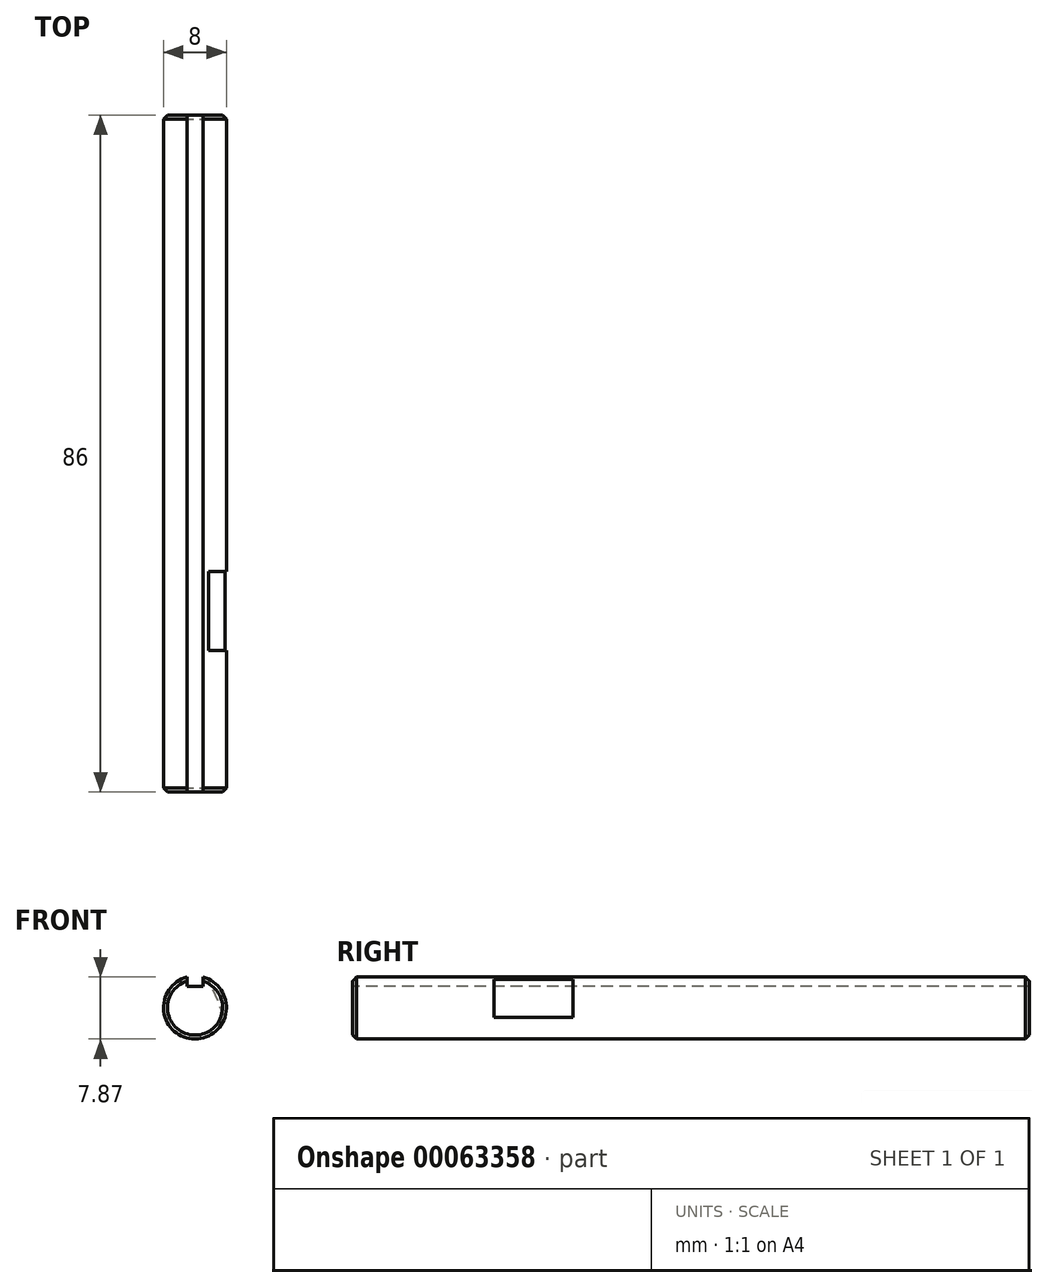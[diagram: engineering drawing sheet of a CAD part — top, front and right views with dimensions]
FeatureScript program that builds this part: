
annotation { "Feature Type Name" : "Feature", "Feature Type Description" : "" }
export const myFeature = defineFeature(function(context is Context, id is Id, definition is map)
    precondition{}
    {
        {
            var Q0;
            Q0=qCreatedBy(makeId("Front.planeOp"),FACE);
            var sketch = newSketch(context, id + "F0", { "sketchPlane" : qUnion([Q0])});
            skCircle(sketch, "E0", {"center": v(0, 0) * mm, "radius": 4 * mm});
            skSolve(sketch);
        }
        {
            var Q0;
            Q0=qSketchRegion(id+"F0",true);
            extrude(context, id + "F1", {"entities" : qUnion([Q0]), "depth" : 86 * mm});
        }
        {
            var Q0;
            Q0=makeQuery(id+"F1.opExtrude","CAP_FACE",FACE,{"disambiguationData":[OSD([sQuery(id+"F0.wireOp",EDGE,"E0")])],"isStart":false});
            var sketch = newSketch(context, id + "F2", { "sketchPlane" : qUnion([Q0])});
            skLineSegment(sketch, "E1", {"start": v(-1, 5.35) * mm, "end": v(1, 5.35) * mm});
            skLineSegment(sketch, "E2", {"start": v(0, 0) * mm, "end": v(0, 5.35) * mm, "construction": true});
            skLineSegment(sketch, "E3", {"start": v(-1, 2.67) * mm, "end": v(1, 2.67) * mm});
            skPoint(sketch, "E3.startSnap0", {"position": v(0, 2.67) * mm});
            skLineSegment(sketch, "E4", {"start": v(1, 2.67) * mm, "end": v(1, 5.35) * mm});
            skLineSegment(sketch, "E5", {"start": v(-1, 2.67) * mm, "end": v(-1, 5.35) * mm});
            skLineSegment(sketch, "E6", {"start": v(1, 3.87) * mm, "end": v(-1, 3.87) * mm, "construction": true});
            skSolve(sketch);
        }
        {
            var Q0;
            Q0=qSketchRegion(id+"F2",true);
            extrude(context, id + "F3", {"entities" : qUnion([Q0]), "operationType" : NewBodyOperationType.REMOVE, "endBound" : BoundingType.THROUGH_ALL, "oppositeDirection" : true, "depth" : 25 * mm});
        }
        {
            var Q0;
            Q0=makeQuery(id+"F1.opExtrude","CAP_EDGE",EDGE,{"disambiguationData":[OSD([sQuery(id+"F0.wireOp",EDGE,"E0")])],"isStart":false});
            var Q1;
            Q1=makeQuery(id+"F1.opExtrude","CAP_EDGE",EDGE,{"disambiguationData":[OSD([sQuery(id+"F0.wireOp",EDGE,"E0")])],"isStart":true});
            chamfer(context, id + "F4", {"entities" : qUnion([Q0, Q1]), "width" : 0.5 * mm, "tangentPropagation" : true});
        }
        {
            var Q0;
            Q0=qCreatedBy(makeId("Top.planeOp"),FACE);
            var Q1;
            Q1=makeQuery(id+"F1.opExtrude","SWEPT_FACE",FACE,{"disambiguationData":[OSD([sQuery(id+"F0.wireOp",EDGE,"E0")])]});
            cPlane(context, id + "F5", {"entities" : qUnion([Q0, Q1]), "cplaneType" : CPlaneType.LINE_ANGLE, "offset" : 150 * mm, "angle" : 67.2 * degree, "width" : 150 * mm, "height" : 150 * mm});
        }
        {
            var Q0;
            Q0=qCreatedBy(id+"F5.planeOp",FACE);
            cPlane(context, id + "F6", {"entities" : qUnion([Q0]), "cplaneType" : CPlaneType.OFFSET, "offset" : 3 * mm, "oppositeDirection" : true, "width" : 150 * mm, "height" : 150 * mm});
        }
        {
            var Q0;
            Q0=qCreatedBy(id+"F6.planeOp",FACE);
            var sketch = newSketch(context, id + "F7", { "sketchPlane" : qUnion([Q0])});
            skLineSegment(sketch, "E7.bottom", {"start": v(68, 8.64) * mm, "end": v(58, 8.64) * mm});
            skLineSegment(sketch, "E7.top", {"start": v(68, -7.44) * mm, "end": v(58, -7.44) * mm});
            skLineSegment(sketch, "E7.left", {"start": v(68, -7.44) * mm, "end": v(68, 8.64) * mm});
            skLineSegment(sketch, "E7.right", {"start": v(58, 8.64) * mm, "end": v(58, -7.44) * mm});
            skSolve(sketch);
        }
        {
            var Q0;
            Q0=qSketchRegion(id+"F7",true);
            extrude(context, id + "F8", {"entities" : qUnion([Q0]), "operationType" : NewBodyOperationType.REMOVE, "endBound" : BoundingType.THROUGH_ALL, "oppositeDirection" : true, "depth" : 25 * mm});
        }
    });
